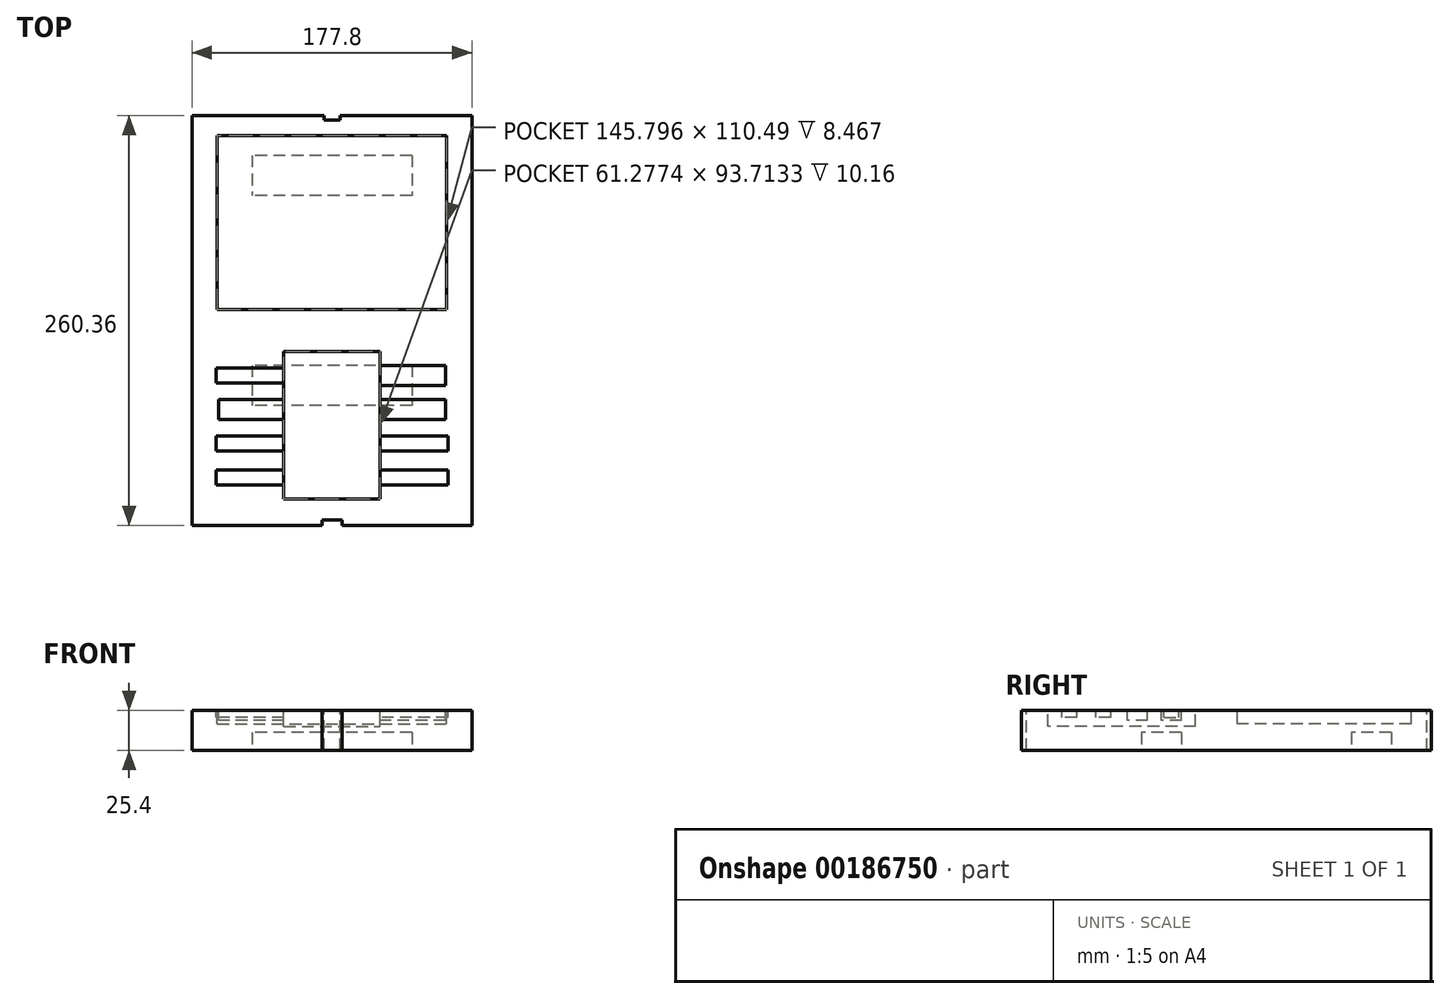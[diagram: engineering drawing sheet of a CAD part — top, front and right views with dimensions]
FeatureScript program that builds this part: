
annotation { "Feature Type Name" : "Feature", "Feature Type Description" : "" }
export const myFeature = defineFeature(function(context is Context, id is Id, definition is map)
    precondition{}
    {
        {
            var Q0;
            Q0=qCreatedBy(makeId("Top.planeOp"),FACE);
            var sketch = newSketch(context, id + "F0", { "sketchPlane" : qUnion([Q0])});
            skLineSegment(sketch, "E0.bottom", {"start": v(88.9, -130.18) * mm, "end": v(-88.9, -130.18) * mm});
            skLineSegment(sketch, "E0.top", {"start": v(88.9, 130.18) * mm, "end": v(-88.9, 130.18) * mm});
            skLineSegment(sketch, "E0.left", {"start": v(88.9, -130.18) * mm, "end": v(88.9, 130.18) * mm});
            skLineSegment(sketch, "E0.right", {"start": v(-88.9, -130.18) * mm, "end": v(-88.9, 130.18) * mm});
            skPoint(sketch, "E0.middle", {"position": v(0, 0) * mm});
            skSolve(sketch);
        }
        {
            var Q0;
            Q0=makeQuery(id+"F0.imprint","IMPRINT",FACE,{"disambiguationData":[TD([[makeQuery(id+"F0.imprint","IMPRINT",EDGE,{"derivedFrom":sQuery(id+"F0.wireOp",EDGE,"E0.bottom")}),-1.0]])]});
            extrude(context, id + "F1", {"entities" : qUnion([Q0]), "depth" : 25.4 * mm});
        }
        {
            var Q0;
            Q0=makeQuery(id+"F1.opExtrude","CAP_FACE",FACE,{"disambiguationData":[OSD([sQuery(id+"F0.wireOp",EDGE,"E0.bottom"),sQuery(id+"F0.wireOp",EDGE,"E0.top"),sQuery(id+"F0.wireOp",EDGE,"E0.left"),sQuery(id+"F0.wireOp",EDGE,"E0.right")])],"isStart":false});
            var sketch = newSketch(context, id + "F2", { "sketchPlane" : qUnion([Q0])});
            skLineSegment(sketch, "E1.bottom", {"start": v(5.08, 127.38) * mm, "end": v(-5.08, 127.38) * mm});
            skLineSegment(sketch, "E1.top", {"start": v(5.08, 132.97) * mm, "end": v(-5.08, 132.97) * mm});
            skLineSegment(sketch, "E1.left", {"start": v(5.08, 127.38) * mm, "end": v(5.08, 132.97) * mm});
            skLineSegment(sketch, "E1.right", {"start": v(-5.08, 127.38) * mm, "end": v(-5.08, 132.97) * mm});
            skPoint(sketch, "E1.middle", {"position": v(0, 130.18) * mm});
            skLineSegment(sketch, "E2.bottom", {"start": v(6.35, -133.48) * mm, "end": v(-6.35, -133.48) * mm});
            skLineSegment(sketch, "E2.top", {"start": v(6.35, -126.87) * mm, "end": v(-6.35, -126.87) * mm});
            skLineSegment(sketch, "E2.left", {"start": v(6.35, -133.48) * mm, "end": v(6.35, -126.87) * mm});
            skLineSegment(sketch, "E2.right", {"start": v(-6.35, -133.48) * mm, "end": v(-6.35, -126.87) * mm});
            skPoint(sketch, "E2.middle", {"position": v(0, -130.18) * mm});
            skSolve(sketch);
        }
        {
            var Q0;
            Q0 = qSketchRegion(id + "F2", true);
            extrude(context, id + "F3", {"entities" : qUnion([Q0]), "operationType" : NewBodyOperationType.REMOVE, "endBound" : BoundingType.THROUGH_ALL, "oppositeDirection" : true, "depth" : 25.4 * mm});
        }
        {
            var Q0;
            Q0=makeQuery(id+"F1.opExtrude","CAP_FACE",FACE,{"disambiguationData":[OSD([sQuery(id+"F0.wireOp",EDGE,"E0.bottom"),sQuery(id+"F0.wireOp",EDGE,"E0.top"),sQuery(id+"F0.wireOp",EDGE,"E0.left"),sQuery(id+"F0.wireOp",EDGE,"E0.right")])],"isStart":false});
            var sketch = newSketch(context, id + "F4", { "sketchPlane" : qUnion([Q0])});
            skLineSegment(sketch, "E3.bottom", {"start": v(-72.9, 117.48) * mm, "end": v(72.9, 117.48) * mm});
            skLineSegment(sketch, "E3.top", {"start": v(-72.9, 6.99) * mm, "end": v(72.9, 6.99) * mm});
            skLineSegment(sketch, "E3.left", {"start": v(-72.9, 117.48) * mm, "end": v(-72.9, 6.99) * mm});
            skLineSegment(sketch, "E3.right", {"start": v(72.9, 117.48) * mm, "end": v(72.9, 6.99) * mm});
            skPoint(sketch, "E3.middle", {"position": v(0, 62.23) * mm});
            skSolve(sketch);
        }
        {
            var Q0;
            Q0 = qSketchRegion(id + "F4", true);
            extrude(context, id + "F5", {"entities" : qUnion([Q0]), "operationType" : NewBodyOperationType.REMOVE, "oppositeDirection" : true, "depth" : 8.47 * mm});
        }
        {
            var Q0;
            Q0=makeQuery(id+"F1.opExtrude","CAP_FACE",FACE,{"disambiguationData":[OSD([sQuery(id+"F0.wireOp",EDGE,"E0.bottom"),sQuery(id+"F0.wireOp",EDGE,"E0.top"),sQuery(id+"F0.wireOp",EDGE,"E0.left"),sQuery(id+"F0.wireOp",EDGE,"E0.right")])],"isStart":false});
            var sketch = newSketch(context, id + "F6", { "sketchPlane" : qUnion([Q0])});
            skLineSegment(sketch, "E4", {"start": v(-88.9, -34.93) * mm, "end": v(88.9, -34.92) * mm, "construction": true});
            skLineSegment(sketch, "E5", {"start": v(-88.9, -56.52) * mm, "end": v(88.9, -56.51) * mm, "construction": true});
            skLineSegment(sketch, "E6", {"start": v(-88.9, -78.1) * mm, "end": v(88.9, -78.1) * mm, "construction": true});
            skLineSegment(sketch, "E7", {"start": v(-88.9, -99.7) * mm, "end": v(88.9, -99.7) * mm, "construction": true});
            skLineSegment(sketch, "E8", {"start": v(-44.45, -34.93) * mm, "end": v(-44.45, -130.18) * mm, "construction": true});
            skLineSegment(sketch, "E9", {"start": v(44.45, -34.93) * mm, "end": v(44.45, -130.18) * mm, "construction": true});
            skPoint(sketch, "E9.endSnap0", {"position": v(47.62, -130.18) * mm});
            skLineSegment(sketch, "E10.bottom", {"start": v(-15.24, -39.69) * mm, "end": v(-73.66, -39.69) * mm});
            skLineSegment(sketch, "E10.top", {"start": v(-15.24, -30.16) * mm, "end": v(-73.66, -30.16) * mm});
            skLineSegment(sketch, "E10.left", {"start": v(-15.24, -39.69) * mm, "end": v(-15.24, -30.16) * mm});
            skLineSegment(sketch, "E10.right", {"start": v(-73.66, -39.69) * mm, "end": v(-73.66, -30.16) * mm});
            skPoint(sketch, "E10.middle", {"position": v(-44.45, -34.93) * mm});
            skLineSegment(sketch, "E11.bottom", {"start": v(-16.83, -62.92) * mm, "end": v(-72.07, -62.92) * mm});
            skLineSegment(sketch, "E11.top", {"start": v(-16.83, -50.11) * mm, "end": v(-72.07, -50.11) * mm});
            skLineSegment(sketch, "E11.left", {"start": v(-16.83, -62.92) * mm, "end": v(-16.83, -50.11) * mm});
            skLineSegment(sketch, "E11.right", {"start": v(-72.07, -62.92) * mm, "end": v(-72.07, -50.11) * mm});
            skPoint(sketch, "E11.middle", {"position": v(-44.45, -56.52) * mm});
            skLineSegment(sketch, "E12.bottom", {"start": v(-15.24, -82.87) * mm, "end": v(-73.66, -82.87) * mm});
            skLineSegment(sketch, "E12.top", {"start": v(-15.24, -73.34) * mm, "end": v(-73.66, -73.34) * mm});
            skLineSegment(sketch, "E12.left", {"start": v(-15.24, -82.87) * mm, "end": v(-15.24, -73.34) * mm});
            skLineSegment(sketch, "E12.right", {"start": v(-73.66, -82.87) * mm, "end": v(-73.66, -73.34) * mm});
            skPoint(sketch, "E12.middle", {"position": v(-44.45, -78.1) * mm});
            skLineSegment(sketch, "E13.bottom", {"start": v(-15.24, -104.46) * mm, "end": v(-73.66, -104.46) * mm});
            skLineSegment(sketch, "E13.top", {"start": v(-15.24, -94.93) * mm, "end": v(-73.66, -94.93) * mm});
            skLineSegment(sketch, "E13.left", {"start": v(-15.24, -104.46) * mm, "end": v(-15.24, -94.93) * mm});
            skLineSegment(sketch, "E13.right", {"start": v(-73.66, -104.46) * mm, "end": v(-73.66, -94.93) * mm});
            skPoint(sketch, "E13.middle", {"position": v(-44.45, -99.7) * mm});
            skLineSegment(sketch, "E14.bottom", {"start": v(72.07, -41.33) * mm, "end": v(16.83, -41.33) * mm});
            skLineSegment(sketch, "E14.top", {"start": v(72.07, -28.52) * mm, "end": v(16.83, -28.52) * mm});
            skLineSegment(sketch, "E14.left", {"start": v(72.07, -41.33) * mm, "end": v(72.07, -28.52) * mm});
            skLineSegment(sketch, "E14.right", {"start": v(16.83, -41.33) * mm, "end": v(16.83, -28.52) * mm});
            skPoint(sketch, "E14.middle", {"position": v(44.45, -34.93) * mm});
            skLineSegment(sketch, "E15.bottom", {"start": v(72.07, -62.92) * mm, "end": v(16.83, -62.92) * mm});
            skLineSegment(sketch, "E15.top", {"start": v(72.07, -50.11) * mm, "end": v(16.83, -50.11) * mm});
            skLineSegment(sketch, "E15.left", {"start": v(72.07, -62.92) * mm, "end": v(72.07, -50.11) * mm});
            skLineSegment(sketch, "E15.right", {"start": v(16.83, -62.92) * mm, "end": v(16.83, -50.11) * mm});
            skPoint(sketch, "E15.middle", {"position": v(44.45, -56.52) * mm});
            skLineSegment(sketch, "E16.bottom", {"start": v(73.66, -82.87) * mm, "end": v(15.24, -82.87) * mm});
            skLineSegment(sketch, "E16.top", {"start": v(73.66, -73.34) * mm, "end": v(15.24, -73.34) * mm});
            skLineSegment(sketch, "E16.left", {"start": v(73.66, -82.87) * mm, "end": v(73.66, -73.34) * mm});
            skLineSegment(sketch, "E16.right", {"start": v(15.24, -82.87) * mm, "end": v(15.24, -73.34) * mm});
            skPoint(sketch, "E16.middle", {"position": v(44.45, -78.1) * mm});
            skLineSegment(sketch, "E17.bottom", {"start": v(73.66, -104.46) * mm, "end": v(15.24, -104.46) * mm});
            skLineSegment(sketch, "E17.top", {"start": v(73.66, -94.93) * mm, "end": v(15.24, -94.93) * mm});
            skLineSegment(sketch, "E17.left", {"start": v(73.66, -104.46) * mm, "end": v(73.66, -94.93) * mm});
            skLineSegment(sketch, "E17.right", {"start": v(15.24, -104.46) * mm, "end": v(15.24, -94.93) * mm});
            skPoint(sketch, "E17.middle", {"position": v(44.45, -99.7) * mm});
            skLineSegment(sketch, "E18.bottom", {"start": v(-30.64, -19.63) * mm, "end": v(30.64, -19.63) * mm});
            skLineSegment(sketch, "E18.top", {"start": v(-30.64, -113.35) * mm, "end": v(30.64, -113.35) * mm});
            skLineSegment(sketch, "E18.left", {"start": v(-30.64, -19.63) * mm, "end": v(-30.64, -113.35) * mm});
            skLineSegment(sketch, "E18.right", {"start": v(30.64, -19.63) * mm, "end": v(30.64, -113.35) * mm});
            skPoint(sketch, "E18.middle", {"position": v(0, -66.5) * mm});
            skPoint(sketch, "E18.middle.positionSnap0", {"position": v(0, -56.52) * mm});
            skPoint(sketch, "E18.centerSnap0", {"position": v(0, -56.52) * mm});
            skSolve(sketch);
        }
        {
            var Q0;
            Q0=makeQuery(id+"F6.imprint","IMPRINT",FACE,{"disambiguationData":[TD([[makeQuery(id+"F6.imprint","IMPRINT",EDGE,{"derivedFrom":sQuery(id+"F6.wireOp",EDGE,"E11.bottom")}),-1.0]])]});
            var Q1;
            Q1=makeQuery(id+"F6.imprint","IMPRINT",FACE,{"disambiguationData":[TD([[makeQuery(id+"F6.imprint","IMPRINT",EDGE,{"derivedFrom":sQuery(id+"F6.wireOp",EDGE,"E15.bottom")}),-1.0]])]});
            var Q2;
            Q2=makeQuery(id+"F6.imprint","IMPRINT",FACE,{"disambiguationData":[TD([[makeQuery(id+"F6.imprint","IMPRINT",EDGE,{"derivedFrom":sQuery(id+"F6.wireOp",EDGE,"E14.bottom")}),-1.0]])]});
            extrude(context, id + "F7", {"entities" : qUnion([Q0, Q1, Q2]), "operationType" : NewBodyOperationType.REMOVE, "oppositeDirection" : true, "depth" : 6.35 * mm});
        }
        {
            var Q0;
            Q0=makeQuery(id+"F6.imprint","IMPRINT",FACE,{"disambiguationData":[TD([[makeQuery(id+"F6.imprint","IMPRINT",EDGE,{"derivedFrom":sQuery(id+"F6.wireOp",EDGE,"E10.bottom")}),-1.0]])]});
            var Q1;
            Q1=makeQuery(id+"F6.imprint","IMPRINT",FACE,{"disambiguationData":[TD([[makeQuery(id+"F6.imprint","IMPRINT",EDGE,{"derivedFrom":sQuery(id+"F6.wireOp",EDGE,"E12.bottom")}),-1.0]])]});
            var Q2;
            Q2=makeQuery(id+"F6.imprint","IMPRINT",FACE,{"disambiguationData":[TD([[makeQuery(id+"F6.imprint","IMPRINT",EDGE,{"derivedFrom":sQuery(id+"F6.wireOp",EDGE,"E13.bottom")}),-1.0]])]});
            var Q3;
            Q3=makeQuery(id+"F6.imprint","IMPRINT",FACE,{"disambiguationData":[TD([[makeQuery(id+"F6.imprint","IMPRINT",EDGE,{"derivedFrom":sQuery(id+"F6.wireOp",EDGE,"E16.bottom")}),-1.0]])]});
            var Q4;
            Q4=makeQuery(id+"F6.imprint","IMPRINT",FACE,{"disambiguationData":[TD([[makeQuery(id+"F6.imprint","IMPRINT",EDGE,{"derivedFrom":sQuery(id+"F6.wireOp",EDGE,"E17.bottom")}),-1.0]])]});
            extrude(context, id + "F8", {"entities" : qUnion([Q0, Q1, Q2, Q3, Q4]), "operationType" : NewBodyOperationType.REMOVE, "oppositeDirection" : true, "depth" : 4.44 * mm});
        }
        {
            var Q0;
            {var subQ16=sQuery(id+"F6.wireOp",EDGE,"E10.left");Q0=makeQuery(id+"F6.imprint","IMPRINT",FACE,{"disambiguationData":[TD([[makeQuery(id+"F6.imprint","IMPRINT",EDGE,{"derivedFrom":subQ16}),-1.0]])]});}
            var Q1;
            {var subQ0=sQuery(id+"F6.wireOp",EDGE,"E10.left");Q1=makeQuery(id+"F6.imprint","IMPRINT",FACE,{"disambiguationData":[TD([[makeQuery(id+"F6.imprint","IMPRINT",EDGE,{"derivedFrom":subQ0}),1.0]])]});}
            var Q2;
            {var subQ0=sQuery(id+"F6.wireOp",EDGE,"E11.left");Q2=makeQuery(id+"F6.imprint","IMPRINT",FACE,{"disambiguationData":[TD([[makeQuery(id+"F6.imprint","IMPRINT",EDGE,{"derivedFrom":subQ0}),1.0]])]});}
            var Q3;
            {var subQ0=sQuery(id+"F6.wireOp",EDGE,"E12.left");Q3=makeQuery(id+"F6.imprint","IMPRINT",FACE,{"disambiguationData":[TD([[makeQuery(id+"F6.imprint","IMPRINT",EDGE,{"derivedFrom":subQ0}),1.0]])]});}
            var Q4;
            {var subQ0=sQuery(id+"F6.wireOp",EDGE,"E13.left");Q4=makeQuery(id+"F6.imprint","IMPRINT",FACE,{"disambiguationData":[TD([[makeQuery(id+"F6.imprint","IMPRINT",EDGE,{"derivedFrom":subQ0}),1.0]])]});}
            var Q5;
            {var subQ0=sQuery(id+"F6.wireOp",EDGE,"E17.right");Q5=makeQuery(id+"F6.imprint","IMPRINT",FACE,{"disambiguationData":[TD([[makeQuery(id+"F6.imprint","IMPRINT",EDGE,{"derivedFrom":subQ0}),-1.0]])]});}
            var Q6;
            {var subQ0=sQuery(id+"F6.wireOp",EDGE,"E16.right");Q6=makeQuery(id+"F6.imprint","IMPRINT",FACE,{"disambiguationData":[TD([[makeQuery(id+"F6.imprint","IMPRINT",EDGE,{"derivedFrom":subQ0}),-1.0]])]});}
            var Q7;
            {var subQ0=sQuery(id+"F6.wireOp",EDGE,"E15.right");Q7=makeQuery(id+"F6.imprint","IMPRINT",FACE,{"disambiguationData":[TD([[makeQuery(id+"F6.imprint","IMPRINT",EDGE,{"derivedFrom":subQ0}),-1.0]])]});}
            var Q8;
            {var subQ0=sQuery(id+"F6.wireOp",EDGE,"E14.right");Q8=makeQuery(id+"F6.imprint","IMPRINT",FACE,{"disambiguationData":[TD([[makeQuery(id+"F6.imprint","IMPRINT",EDGE,{"derivedFrom":subQ0}),-1.0]])]});}
            var Q9;
            Q9=sQuery(id+"F6.wireOp",EDGE,"E18.left");
            var Q10;
            Q10=sQuery(id+"F6.wireOp",EDGE,"E18.bottom");
            var Q11;
            Q11=sQuery(id+"F6.wireOp",EDGE,"E18.right");
            var Q12;
            Q12=sQuery(id+"F6.wireOp",EDGE,"E18.top");
            extrude(context, id + "F9", {"entities" : qUnion([Q0, Q1, Q2, Q3, Q4, Q5, Q6, Q7, Q8]), "operationType" : NewBodyOperationType.REMOVE, "surfaceEntities" : qUnion([Q9, Q10, Q11, Q12]), "oppositeDirection" : true, "depth" : 10.16 * mm});
        }
        {
            var Q0;
            Q0=makeQuery(id+"F1.opExtrude","CAP_FACE",FACE,{"disambiguationData":[OSD([sQuery(id+"F0.wireOp",EDGE,"E0.bottom"),sQuery(id+"F0.wireOp",EDGE,"E0.top"),sQuery(id+"F0.wireOp",EDGE,"E0.left"),sQuery(id+"F0.wireOp",EDGE,"E0.right")])],"isStart":true});
            var sketch = newSketch(context, id + "F10", { "sketchPlane" : qUnion([Q0])});
            skLineSegment(sketch, "E19.bottom", {"start": v(50.8, -104.78) * mm, "end": v(-50.8, -104.78) * mm});
            skLineSegment(sketch, "E19.top", {"start": v(50.8, -79.38) * mm, "end": v(-50.8, -79.38) * mm});
            skLineSegment(sketch, "E19.left", {"start": v(50.8, -104.78) * mm, "end": v(50.8, -79.38) * mm});
            skLineSegment(sketch, "E19.right", {"start": v(-50.8, -104.78) * mm, "end": v(-50.8, -79.38) * mm});
            skPoint(sketch, "E19.middle", {"position": v(0, -92.08) * mm});
            skLineSegment(sketch, "E20.bottom", {"start": v(50.8, 28.57) * mm, "end": v(-50.8, 28.57) * mm});
            skLineSegment(sketch, "E20.top", {"start": v(50.8, 53.98) * mm, "end": v(-50.8, 53.98) * mm});
            skLineSegment(sketch, "E20.left", {"start": v(50.8, 28.58) * mm, "end": v(50.8, 53.98) * mm});
            skLineSegment(sketch, "E20.right", {"start": v(-50.8, 28.57) * mm, "end": v(-50.8, 53.98) * mm});
            skPoint(sketch, "E20.middle", {"position": v(0, 41.28) * mm});
            skSolve(sketch);
        }
        {
            var Q0;
            Q0=makeQuery(id+"F10.imprint","IMPRINT",FACE,{"disambiguationData":[TD([[makeQuery(id+"F10.imprint","IMPRINT",EDGE,{"derivedFrom":sQuery(id+"F10.wireOp",EDGE,"E20.bottom")}),-1.0]])]});
            var Q1;
            Q1=makeQuery(id+"F10.imprint","IMPRINT",FACE,{"disambiguationData":[TD([[makeQuery(id+"F10.imprint","IMPRINT",EDGE,{"derivedFrom":sQuery(id+"F10.wireOp",EDGE,"E19.bottom")}),-1.0]])]});
            extrude(context, id + "F11", {"entities" : qUnion([Q0, Q1]), "operationType" : NewBodyOperationType.REMOVE, "oppositeDirection" : true, "depth" : 11.43 * mm});
        }
    });
